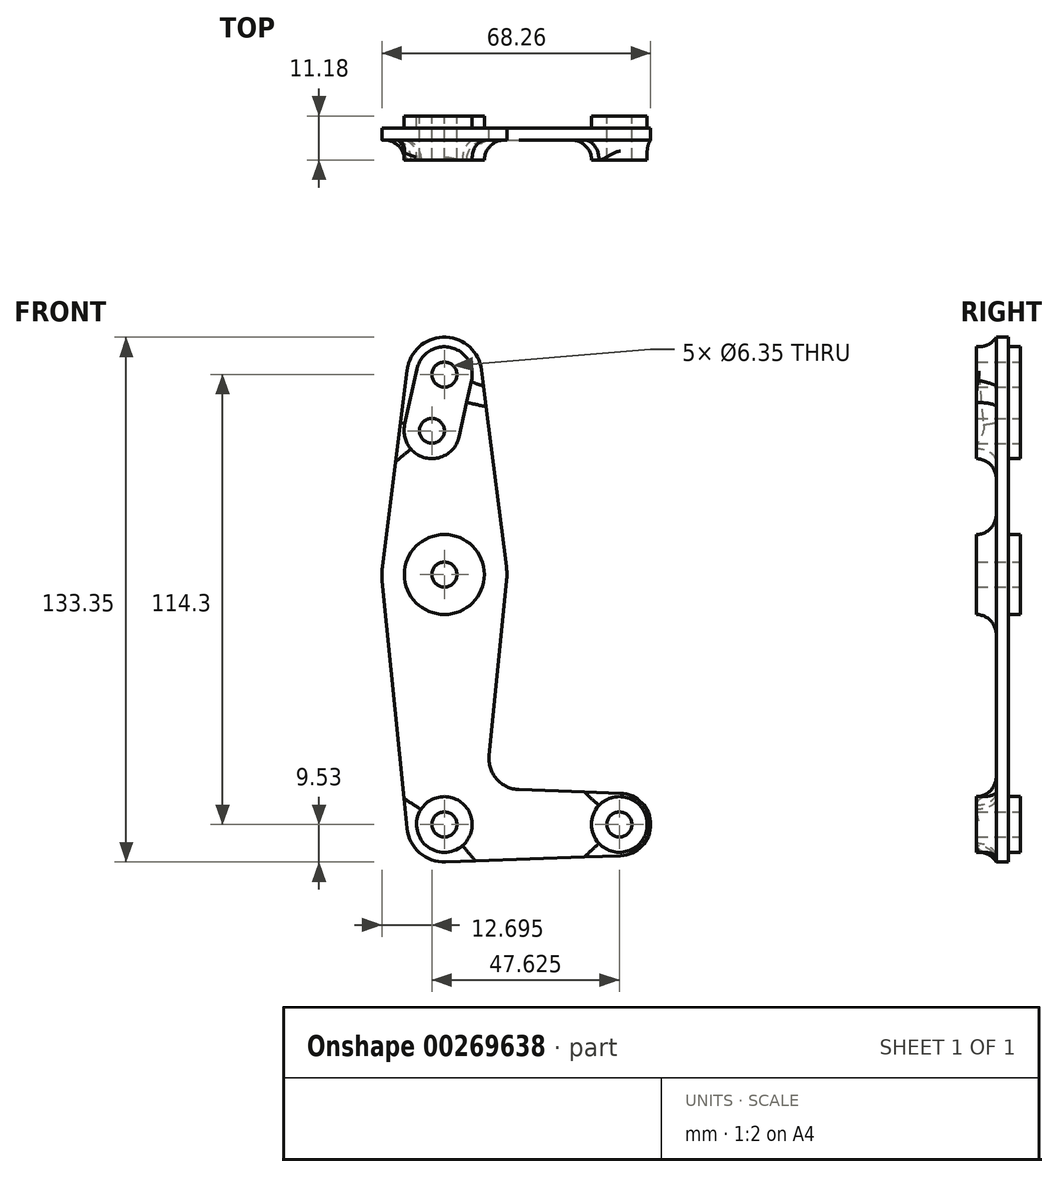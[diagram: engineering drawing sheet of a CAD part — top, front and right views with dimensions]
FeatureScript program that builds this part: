
annotation { "Feature Type Name" : "Feature", "Feature Type Description" : "" }
export const myFeature = defineFeature(function(context is Context, id is Id, definition is map)
    precondition{}
    {
        {
            var Q0;
            Q0=qCreatedBy(makeId("Front.planeOp"),FACE);
            var sketch = newSketch(context, id + "F0", { "sketchPlane" : qUnion([Q0])});
            skLineSegment(sketch, "E0", {"start": v(0, 50.8) * mm, "end": v(0, -63.5) * mm, "construction": true});
            skLineSegment(sketch, "E1", {"start": v(0, -63.5) * mm, "end": v(44.45, -63.5) * mm, "construction": true});
            skCircle(sketch, "E2", {"center": v(0, 50.8) * mm, "radius": 9.53 * mm});
            skCircle(sketch, "E3", {"center": v(0, 0) * mm, "radius": 15.88 * mm});
            skCircle(sketch, "E4", {"center": v(0, -63.5) * mm, "radius": 9.53 * mm});
            skCircle(sketch, "E5", {"center": v(44.45, -63.5) * mm, "radius": 7.94 * mm});
            skLineSegment(sketch, "E6", {"start": v(9.45, 52) * mm, "end": v(15.75, 1.98) * mm});
            skLineSegment(sketch, "E7", {"start": v(-9.45, 52) * mm, "end": v(-15.75, 1.98) * mm});
            skLineSegment(sketch, "E8", {"start": v(-15.8, -1.59) * mm, "end": v(-9.48, -64.45) * mm});
            skLineSegment(sketch, "E9", {"start": v(-9.48, -64.45) * mm, "end": v(-9.27, -63.03) * mm});
            skLineSegment(sketch, "E10", {"start": v(15.8, -1.59) * mm, "end": v(11.34, -45.9) * mm});
            skLineSegment(sketch, "E11", {"start": v(9.57, -63.5) * mm, "end": v(8.7, -62.32) * mm});
            skLineSegment(sketch, "E12", {"start": v(18.97, -54.65) * mm, "end": v(44.73, -55.57) * mm});
            skLineSegment(sketch, "E13", {"start": v(0.34, -73.02) * mm, "end": v(44.73, -71.43) * mm});
            skLineSegment(sketch, "E14", {"start": v(44.73, -71.43) * mm, "end": v(44.83, -70.3) * mm});
            skCircle(sketch, "E15", {"center": v(0, 50.8) * mm, "radius": 3.18 * mm});
            skCircle(sketch, "E16", {"center": v(-3.17, 36.53) * mm, "radius": 3.18 * mm});
            skCircle(sketch, "E17", {"center": v(0, 0) * mm, "radius": 3.18 * mm});
            skCircle(sketch, "E18", {"center": v(0, -63.5) * mm, "radius": 3.18 * mm});
            skCircle(sketch, "E19", {"center": v(44.45, -63.5) * mm, "radius": 3.18 * mm});
            skArc(sketch, "E20.filletArc", {"start": v(11.34, -45.9) * mm, "mid": v(13.26, -51.93) * mm, "end": v(18.97, -54.65) * mm});
            skSolve(sketch);
        }
        {
            var Q0;
            Q0=makeQuery(id+"F0.imprint","IMPRINT",FACE,{"disambiguationData":[TD([[makeQuery(id+"F0.imprint","IMPRINT",EDGE,{"derivedFrom":sQuery(id+"F0.wireOp",EDGE,"E15")}),-1.0]])]});
            var Q1;
            Q1=makeQuery(id+"F0.imprint","IMPRINT",FACE,{"disambiguationData":[TD([[makeQuery(id+"F0.imprint","IMPRINT",EDGE,{"derivedFrom":sQuery(id+"F0.wireOp",EDGE,"E18")}),-1.0]])]});
            var Q2;
            Q2=makeQuery(id+"F0.imprint","IMPRINT",FACE,{"disambiguationData":[TD([[makeQuery(id+"F0.imprint","IMPRINT",EDGE,{"derivedFrom":sQuery(id+"F0.wireOp",EDGE,"E19")}),-1.0]])]});
            var Q3;
            {var subQ1=sQuery(id+"F0.wireOp",EDGE,"E6");Q3=makeQuery(id+"F0.imprint","IMPRINT",FACE,{"disambiguationData":[TD([[makeQuery(id+"F0.imprint","IMPRINT",EDGE,{"derivedFrom":subQ1}),-1.0]])]});}
            var Q4;
            Q4=makeQuery(id+"F0.imprint","IMPRINT",FACE,{"disambiguationData":[TD([[makeQuery(id+"F0.imprint","IMPRINT",EDGE,{"derivedFrom":sQuery(id+"F0.wireOp",EDGE,"E17")}),-1.0]])]});
            var Q5;
            {var subQ5=sQuery(id+"F0.wireOp",EDGE,"E8");Q5=makeQuery(id+"F0.imprint","IMPRINT",FACE,{"disambiguationData":[TD([[makeQuery(id+"F0.imprint","IMPRINT",EDGE,{"derivedFrom":subQ5}),1.0]])]});}
            extrude(context, id + "F1", {"entities" : qUnion([Q0, Q1, Q2, Q3, Q4, Q5]), "depth" : 3.05 * mm});
        }
        {
            var Q0;
            Q0=makeQuery(id+"F1.opExtrude","CAP_FACE",FACE,{"disambiguationData":[OSD([sQuery(id+"F0.wireOp",EDGE,"E2"),sQuery(id+"F0.wireOp",EDGE,"E3"),sQuery(id+"F0.wireOp",EDGE,"E4"),sQuery(id+"F0.wireOp",EDGE,"E5"),sQuery(id+"F0.wireOp",EDGE,"E6"),sQuery(id+"F0.wireOp",EDGE,"E7"),sQuery(id+"F0.wireOp",EDGE,"E8"),sQuery(id+"F0.wireOp",EDGE,"E10"),sQuery(id+"F0.wireOp",EDGE,"E12"),sQuery(id+"F0.wireOp",EDGE,"E13"),sQuery(id+"F0.wireOp",EDGE,"E15"),sQuery(id+"F0.wireOp",EDGE,"E16"),sQuery(id+"F0.wireOp",EDGE,"E17"),sQuery(id+"F0.wireOp",EDGE,"E18"),sQuery(id+"F0.wireOp",EDGE,"E19"),sQuery(id+"F0.wireOp",EDGE,"E20.filletArc")])],"isStart":false});
            var sketch = newSketch(context, id + "F2", { "sketchPlane" : qUnion([Q0])});
            skCircle(sketch, "E21", {"center": v(0, 0) * mm, "radius": 10.16 * mm});
            skArc(sketch, "E22", {"start": v(6.9, 49.26) * mm, "mid": v(1.54, 57.7) * mm, "end": v(-6.9, 52.34) * mm});
            skCircle(sketch, "E23", {"center": v(0, -63.5) * mm, "radius": 7.07 * mm});
            skCircle(sketch, "E24", {"center": v(44.45, -63.5) * mm, "radius": 7.07 * mm});
            skArc(sketch, "E25", {"start": v(-10.08, 38.06) * mm, "mid": v(-4.71, 29.62) * mm, "end": v(3.73, 34.99) * mm});
            skLineSegment(sketch, "E26", {"start": v(-10.08, 38.06) * mm, "end": v(-6.9, 52.34) * mm});
            skLineSegment(sketch, "E27", {"start": v(3.73, 34.99) * mm, "end": v(6.9, 49.26) * mm});
            skSolve(sketch);
        }
        {
            var Q0;
            Q0=makeQuery(id+"F2.imprint","IMPRINT",FACE,{"disambiguationData":[TD([[makeQuery(id+"F2.imprint","IMPRINT",EDGE,{"derivedFrom":sQuery(id+"F2.wireOp",EDGE,"E22")}),1.0]])]});
            var Q1;
            Q1=makeQuery(id+"F2.imprint","IMPRINT",FACE,{"disambiguationData":[TD([[makeQuery(id+"F2.imprint","IMPRINT",EDGE,{"derivedFrom":sQuery(id+"F2.wireOp",EDGE,"E21")}),1.0]])]});
            var Q2;
            Q2=makeQuery(id+"F2.imprint","IMPRINT",FACE,{"disambiguationData":[TD([[makeQuery(id+"F2.imprint","IMPRINT",EDGE,{"derivedFrom":sQuery(id+"F2.wireOp",EDGE,"E23")}),1.0]])]});
            var Q3;
            Q3=makeQuery(id+"F2.imprint","IMPRINT",FACE,{"disambiguationData":[TD([[makeQuery(id+"F2.imprint","IMPRINT",EDGE,{"derivedFrom":sQuery(id+"F2.wireOp",EDGE,"E24")}),1.0]])]});
            extrude(context, id + "F3", {"entities" : qUnion([Q0, Q1, Q2, Q3]), "operationType" : NewBodyOperationType.ADD, "depth" : 5.08 * mm, "hasSecondDirection" : true, "secondDirectionOppositeDirection" : true, "secondDirectionDepth" : 6.1 * mm});
        }
        {
            var Q0;
            Q0=makeQuery(id+"F3.boolean.opBoolean","INTERSECT",EDGE,{"derivedFrom":[makeQuery(id+"F1.opExtrude","CAP_FACE",FACE,{"disambiguationData":[OSD([sQuery(id+"F0.wireOp",EDGE,"E2"),sQuery(id+"F0.wireOp",EDGE,"E3"),sQuery(id+"F0.wireOp",EDGE,"E4"),sQuery(id+"F0.wireOp",EDGE,"E5"),sQuery(id+"F0.wireOp",EDGE,"E6"),sQuery(id+"F0.wireOp",EDGE,"E7"),sQuery(id+"F0.wireOp",EDGE,"E8"),sQuery(id+"F0.wireOp",EDGE,"E10"),sQuery(id+"F0.wireOp",EDGE,"E12"),sQuery(id+"F0.wireOp",EDGE,"E13"),sQuery(id+"F0.wireOp",EDGE,"E15"),sQuery(id+"F0.wireOp",EDGE,"E16"),sQuery(id+"F0.wireOp",EDGE,"E17"),sQuery(id+"F0.wireOp",EDGE,"E18"),sQuery(id+"F0.wireOp",EDGE,"E19"),sQuery(id+"F0.wireOp",EDGE,"E20.filletArc")])],"isStart":false}),makeQuery(id+"F3.opExtrude","SWEPT_FACE",FACE,{"disambiguationData":[OSD([sQuery(id+"F2.wireOp",EDGE,"E25")])]})]});
            var Q1;
            Q1=makeQuery(id+"F3.boolean.opBoolean","INTERSECT",EDGE,{"derivedFrom":[makeQuery(id+"F1.opExtrude","CAP_FACE",FACE,{"disambiguationData":[OSD([sQuery(id+"F0.wireOp",EDGE,"E2"),sQuery(id+"F0.wireOp",EDGE,"E3"),sQuery(id+"F0.wireOp",EDGE,"E4"),sQuery(id+"F0.wireOp",EDGE,"E5"),sQuery(id+"F0.wireOp",EDGE,"E6"),sQuery(id+"F0.wireOp",EDGE,"E7"),sQuery(id+"F0.wireOp",EDGE,"E8"),sQuery(id+"F0.wireOp",EDGE,"E10"),sQuery(id+"F0.wireOp",EDGE,"E12"),sQuery(id+"F0.wireOp",EDGE,"E13"),sQuery(id+"F0.wireOp",EDGE,"E15"),sQuery(id+"F0.wireOp",EDGE,"E16"),sQuery(id+"F0.wireOp",EDGE,"E17"),sQuery(id+"F0.wireOp",EDGE,"E18"),sQuery(id+"F0.wireOp",EDGE,"E19"),sQuery(id+"F0.wireOp",EDGE,"E20.filletArc")])],"isStart":false}),makeQuery(id+"F3.opExtrude","SWEPT_FACE",FACE,{"disambiguationData":[OSD([sQuery(id+"F2.wireOp",EDGE,"E21")])]})]});
            var Q2;
            Q2=makeQuery(id+"F3.boolean.opBoolean","INTERSECT",EDGE,{"derivedFrom":[makeQuery(id+"F1.opExtrude","CAP_FACE",FACE,{"disambiguationData":[OSD([sQuery(id+"F0.wireOp",EDGE,"E2"),sQuery(id+"F0.wireOp",EDGE,"E3"),sQuery(id+"F0.wireOp",EDGE,"E4"),sQuery(id+"F0.wireOp",EDGE,"E5"),sQuery(id+"F0.wireOp",EDGE,"E6"),sQuery(id+"F0.wireOp",EDGE,"E7"),sQuery(id+"F0.wireOp",EDGE,"E8"),sQuery(id+"F0.wireOp",EDGE,"E10"),sQuery(id+"F0.wireOp",EDGE,"E12"),sQuery(id+"F0.wireOp",EDGE,"E13"),sQuery(id+"F0.wireOp",EDGE,"E15"),sQuery(id+"F0.wireOp",EDGE,"E16"),sQuery(id+"F0.wireOp",EDGE,"E17"),sQuery(id+"F0.wireOp",EDGE,"E18"),sQuery(id+"F0.wireOp",EDGE,"E19"),sQuery(id+"F0.wireOp",EDGE,"E20.filletArc")])],"isStart":false}),makeQuery(id+"F3.opExtrude","SWEPT_FACE",FACE,{"disambiguationData":[OSD([sQuery(id+"F2.wireOp",EDGE,"E23")])]})]});
            var Q3;
            Q3=makeQuery(id+"F3.boolean.opBoolean","INTERSECT",EDGE,{"derivedFrom":[makeQuery(id+"F1.opExtrude","CAP_FACE",FACE,{"disambiguationData":[OSD([sQuery(id+"F0.wireOp",EDGE,"E2"),sQuery(id+"F0.wireOp",EDGE,"E3"),sQuery(id+"F0.wireOp",EDGE,"E4"),sQuery(id+"F0.wireOp",EDGE,"E5"),sQuery(id+"F0.wireOp",EDGE,"E6"),sQuery(id+"F0.wireOp",EDGE,"E7"),sQuery(id+"F0.wireOp",EDGE,"E8"),sQuery(id+"F0.wireOp",EDGE,"E10"),sQuery(id+"F0.wireOp",EDGE,"E12"),sQuery(id+"F0.wireOp",EDGE,"E13"),sQuery(id+"F0.wireOp",EDGE,"E15"),sQuery(id+"F0.wireOp",EDGE,"E16"),sQuery(id+"F0.wireOp",EDGE,"E17"),sQuery(id+"F0.wireOp",EDGE,"E18"),sQuery(id+"F0.wireOp",EDGE,"E19"),sQuery(id+"F0.wireOp",EDGE,"E20.filletArc")])],"isStart":false}),makeQuery(id+"F3.opExtrude","SWEPT_FACE",FACE,{"disambiguationData":[OSD([sQuery(id+"F2.wireOp",EDGE,"E24")])]})]});
            var Q4;
            Q4=makeQuery(id+"F3.boolean.opBoolean","INTERSECT",EDGE,{"derivedFrom":[makeQuery(id+"F1.opExtrude","CAP_FACE",FACE,{"disambiguationData":[OSD([sQuery(id+"F0.wireOp",EDGE,"E2"),sQuery(id+"F0.wireOp",EDGE,"E3"),sQuery(id+"F0.wireOp",EDGE,"E4"),sQuery(id+"F0.wireOp",EDGE,"E5"),sQuery(id+"F0.wireOp",EDGE,"E6"),sQuery(id+"F0.wireOp",EDGE,"E7"),sQuery(id+"F0.wireOp",EDGE,"E8"),sQuery(id+"F0.wireOp",EDGE,"E10"),sQuery(id+"F0.wireOp",EDGE,"E12"),sQuery(id+"F0.wireOp",EDGE,"E13"),sQuery(id+"F0.wireOp",EDGE,"E15"),sQuery(id+"F0.wireOp",EDGE,"E16"),sQuery(id+"F0.wireOp",EDGE,"E17"),sQuery(id+"F0.wireOp",EDGE,"E18"),sQuery(id+"F0.wireOp",EDGE,"E19"),sQuery(id+"F0.wireOp",EDGE,"E20.filletArc")])],"isStart":false}),makeQuery(id+"F3.opExtrude","SWEPT_FACE",FACE,{"disambiguationData":[OSD([sQuery(id+"F2.wireOp",EDGE,"E22")])]})]});
            var Q5;
            Q5=makeQuery(id+"F3.boolean.opBoolean","INTERSECT",EDGE,{"derivedFrom":[makeQuery(id+"F1.opExtrude","CAP_FACE",FACE,{"disambiguationData":[OSD([sQuery(id+"F0.wireOp",EDGE,"E2"),sQuery(id+"F0.wireOp",EDGE,"E3"),sQuery(id+"F0.wireOp",EDGE,"E4"),sQuery(id+"F0.wireOp",EDGE,"E5"),sQuery(id+"F0.wireOp",EDGE,"E6"),sQuery(id+"F0.wireOp",EDGE,"E7"),sQuery(id+"F0.wireOp",EDGE,"E8"),sQuery(id+"F0.wireOp",EDGE,"E10"),sQuery(id+"F0.wireOp",EDGE,"E12"),sQuery(id+"F0.wireOp",EDGE,"E13"),sQuery(id+"F0.wireOp",EDGE,"E15"),sQuery(id+"F0.wireOp",EDGE,"E16"),sQuery(id+"F0.wireOp",EDGE,"E17"),sQuery(id+"F0.wireOp",EDGE,"E18"),sQuery(id+"F0.wireOp",EDGE,"E19"),sQuery(id+"F0.wireOp",EDGE,"E20.filletArc")])],"isStart":false}),makeQuery(id+"F3.opExtrude","SWEPT_FACE",FACE,{"disambiguationData":[OSD([sQuery(id+"F2.wireOp",EDGE,"E26")])]})]});
            fillet(context, id + "F4", {"entities" : qUnion([Q0, Q1, Q2, Q3, Q4, Q5]), "radius" : 5.08 * mm, "tangentPropagation" : true, "allowEdgeOverflow" : false});
        }
    });
